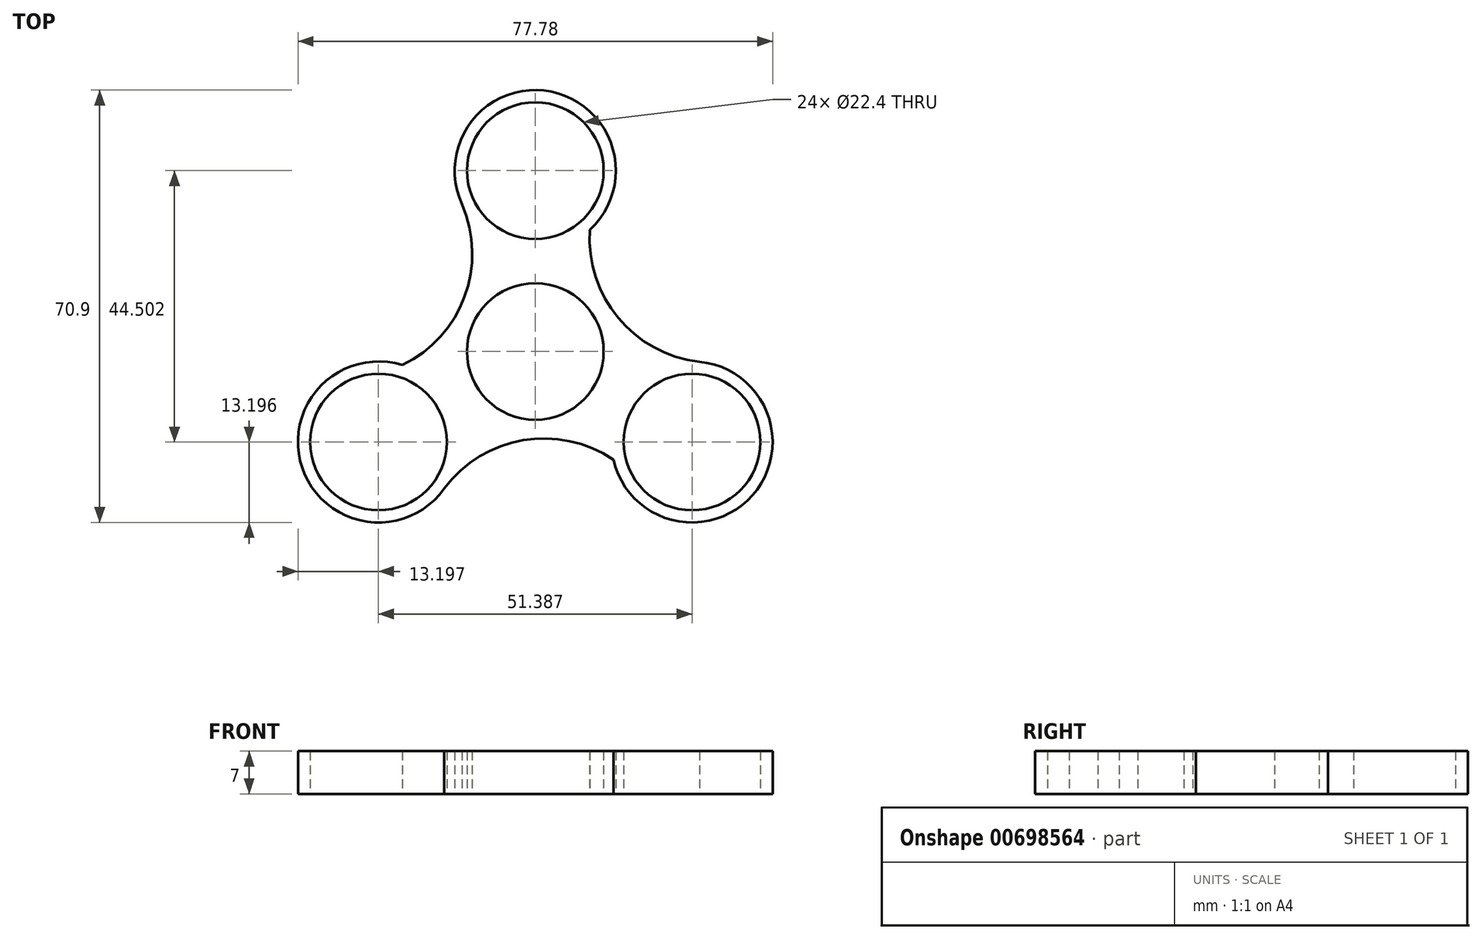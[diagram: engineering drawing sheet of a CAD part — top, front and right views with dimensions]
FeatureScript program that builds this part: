
annotation { "Feature Type Name" : "Feature", "Feature Type Description" : "" }
export const myFeature = defineFeature(function(context is Context, id is Id, definition is map)
    precondition{}
    {
        {
            var Q0;
            Q0=qCreatedBy(makeId("Top.planeOp"),FACE);
            var sketch = newSketch(context, id + "F0", { "sketchPlane" : qUnion([Q0])});
            skCircle(sketch, "E0", {"center": v(0, 0) * mm, "radius": 11.2 * mm});
            skCircle(sketch, "E1", {"center": v(0, 29.67) * mm, "radius": 11.2 * mm});
            skArc(sketch, "E2", {"start": v(8.96, 19.98) * mm, "mid": v(2.58, 42.61) * mm, "end": v(-12, 24.16) * mm});
            skArc(sketch, "E3.1.0", {"start": v(-21.78, -2.23) * mm, "mid": v(-38.2, -19.07) * mm, "end": v(-14.92, -22.47) * mm});
            skCircle(sketch, "E3.1.1", {"center": v(-25.7, -14.83) * mm, "radius": 11.2 * mm});
            skArc(sketch, "E3.2.0", {"start": v(12.82, -17.75) * mm, "mid": v(35.61, -23.54) * mm, "end": v(26.92, -1.7) * mm});
            skCircle(sketch, "E3.2.1", {"center": v(25.7, -14.83) * mm, "radius": 11.2 * mm});
            skArc(sketch, "E4", {"start": v(-21.78, -2.23) * mm, "mid": v(-11.6, 9) * mm, "end": v(-12, 24.16) * mm});
            skArc(sketch, "E5.1.0", {"start": v(12.82, -17.75) * mm, "mid": v(-2, -14.54) * mm, "end": v(-14.92, -22.47) * mm});
            skArc(sketch, "E5.2.0", {"start": v(8.96, 19.98) * mm, "mid": v(13.6, 5.54) * mm, "end": v(26.92, -1.7) * mm});
            skSolve(sketch);
        }
        {
            var Q0;
            Q0=makeQuery(id+"F0.imprint","IMPRINT",FACE,{"disambiguationData":[TD([[makeQuery(id+"F0.imprint","IMPRINT",EDGE,{"derivedFrom":sQuery(id+"F0.wireOp",EDGE,"E0")}),-1.0]])]});
            extrude(context, id + "F1", {"entities" : qUnion([Q0]), "depth" : 7 * mm, "offsetDistance" : 25 * mm});
        }
    });
